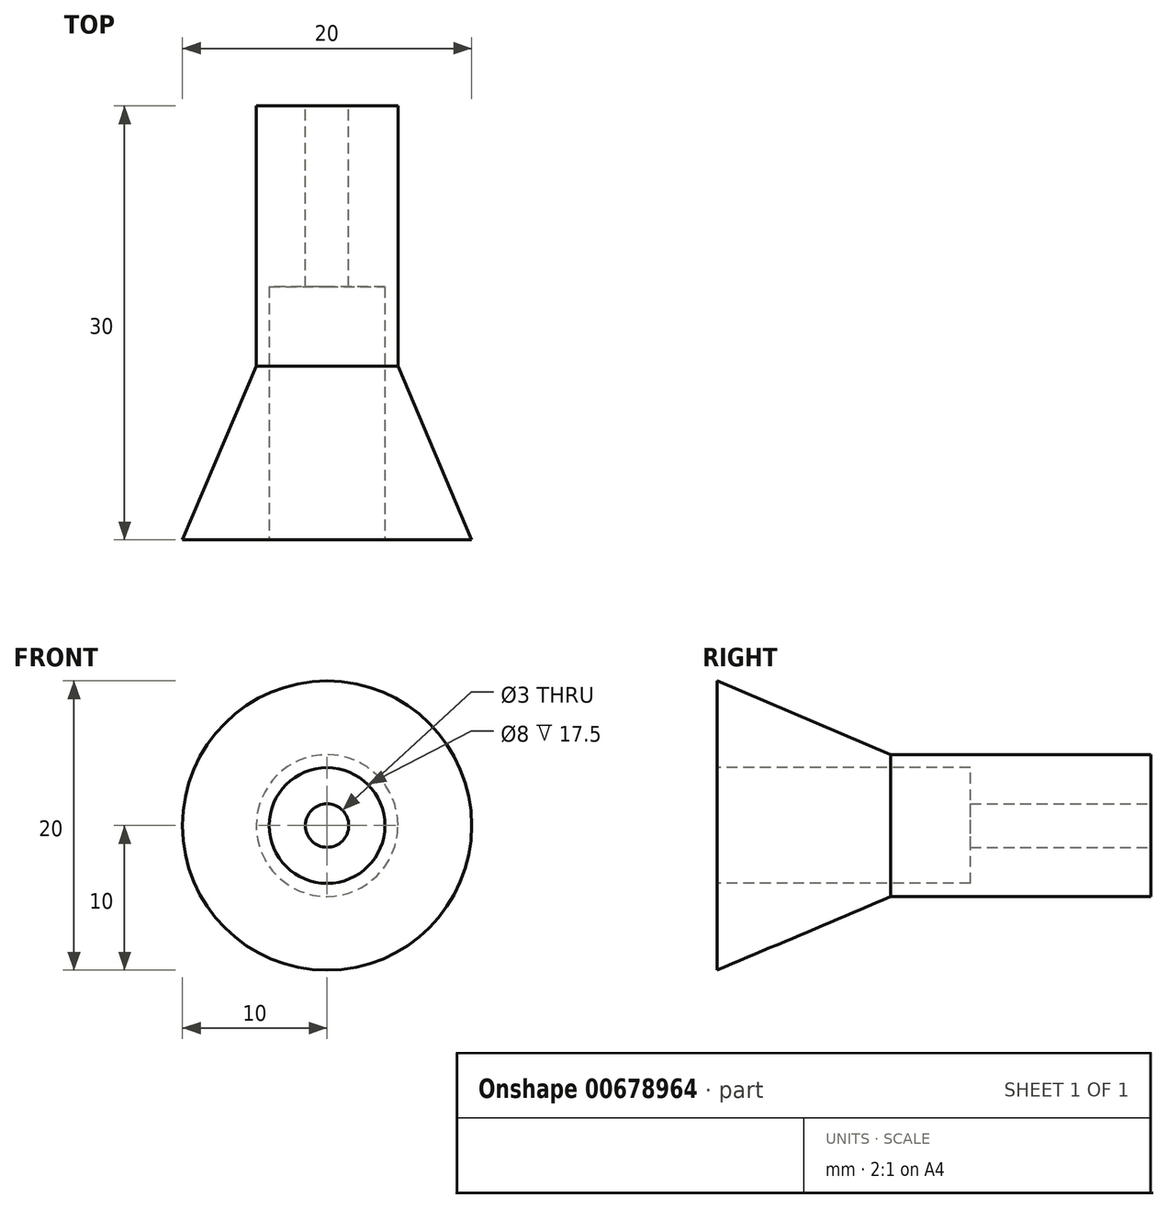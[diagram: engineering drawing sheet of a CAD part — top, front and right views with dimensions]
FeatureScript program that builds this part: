
annotation { "Feature Type Name" : "Feature", "Feature Type Description" : "" }
export const myFeature = defineFeature(function(context is Context, id is Id, definition is map)
    precondition{}
    {
        {
            var Q0;
            Q0=qCreatedBy(makeId("Front.planeOp"),FACE);
            var sketch = newSketch(context, id + "F0", { "sketchPlane" : qUnion([Q0])});
            skCircle(sketch, "E0", {"center": v(0, 0) * mm, "radius": 4.9 * mm});
            skSolve(sketch);
        }
        {
            var Q0;
            Q0 = qSketchRegion(id + "F0", true);
            extrude(context, id + "F1", {"entities" : qUnion([Q0]), "depth" : 18 * mm, "offsetDistance" : 25 * mm});
        }
        {
            var Q0;
            Q0=makeQuery(id+"F1.opExtrude","CAP_FACE",FACE,{"disambiguationData":[OSD([sQuery(id+"F0.wireOp",EDGE,"E0")])],"isStart":false});
            cPlane(context, id + "F2", {"entities" : qUnion([Q0]), "cplaneType" : CPlaneType.OFFSET, "offset" : 12 * mm, "width" : 150 * mm, "height" : 150 * mm});
        }
        {
            var Q0;
            Q0=qCreatedBy(id+"F2.planeOp",FACE);
            var sketch = newSketch(context, id + "F3", { "sketchPlane" : qUnion([Q0])});
            skCircle(sketch, "E1", {"center": v(0, 0) * mm, "radius": 10 * mm});
            skSolve(sketch);
        }
        {
            var Q1;
            Q1=makeQuery(id+"F1.opExtrude","CAP_FACE",FACE,{"disambiguationData":[OSD([sQuery(id+"F0.wireOp",EDGE,"E0")])],"isStart":false});
            var Q2;
            Q2=makeQuery(id+"F3.imprint","IMPRINT",FACE,{"disambiguationData":[TD([[makeQuery(id+"F3.imprint","IMPRINT",EDGE,{"derivedFrom":sQuery(id+"F3.wireOp",EDGE,"E1")}),1.0]])]});
            loft(context, id + "F4", {"operationType" : NewBodyOperationType.ADD, "sheetProfilesArray" : [{ "sheetProfileEntities" : qUnion([Q1]) }, { "sheetProfileEntities" : qUnion([Q2]) }]});
        }
        {
            var Q0;
            Q0=makeQuery(id+"F1.opExtrude","CAP_FACE",FACE,{"disambiguationData":[OSD([sQuery(id+"F0.wireOp",EDGE,"E0")])],"isStart":true});
            var sketch = newSketch(context, id + "F5", { "sketchPlane" : qUnion([Q0])});
            skCircle(sketch, "E2", {"center": v(0, 0) * mm, "radius": 1.5 * mm});
            skSolve(sketch);
        }
        {
            var Q0;
            Q0=makeQuery(id+"F5.imprint","IMPRINT",FACE,{"disambiguationData":[TD([[makeQuery(id+"F5.imprint","IMPRINT",EDGE,{"derivedFrom":sQuery(id+"F5.wireOp",EDGE,"E2")}),1.0]])]});
            extrude(context, id + "F6", {"entities" : qUnion([Q0]), "operationType" : NewBodyOperationType.REMOVE, "oppositeDirection" : true, "depth" : 15 * mm, "offsetDistance" : 25 * mm});
        }
        {
            var Q0;
            Q0=makeQuery(id+"F4.opLoft","CAP_FACE",FACE,{"disambiguationData":[OSD([makeQuery(id+"F3.imprint","IMPRINT",FACE,{"disambiguationData":[TD([[makeQuery(id+"F3.imprint","IMPRINT",EDGE,{"derivedFrom":sQuery(id+"F3.wireOp",EDGE,"E1")}),1.0]])]})])],"isStart":true});
            var sketch = newSketch(context, id + "F7", { "sketchPlane" : qUnion([Q0])});
            skCircle(sketch, "E3", {"center": v(0, 0) * mm, "radius": 4 * mm});
            skSolve(sketch);
        }
        {
            var Q0;
            Q0=makeQuery(id+"F7.imprint","IMPRINT",FACE,{"disambiguationData":[TD([[makeQuery(id+"F7.imprint","IMPRINT",EDGE,{"derivedFrom":sQuery(id+"F7.wireOp",EDGE,"E3")}),1.0]])]});
            extrude(context, id + "F8", {"entities" : qUnion([Q0]), "operationType" : NewBodyOperationType.REMOVE, "oppositeDirection" : true, "depth" : 17.5 * mm, "offsetDistance" : 25 * mm});
        }
    });
